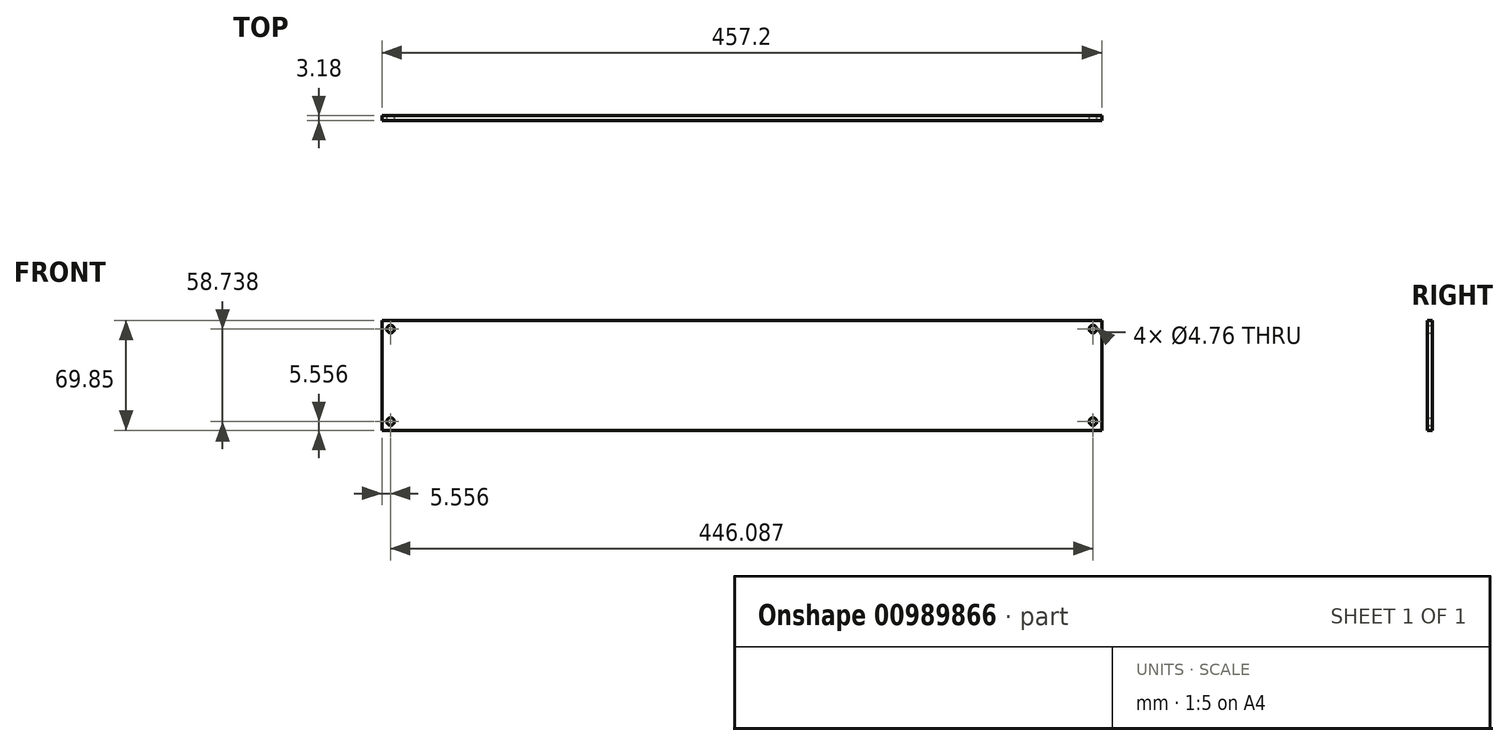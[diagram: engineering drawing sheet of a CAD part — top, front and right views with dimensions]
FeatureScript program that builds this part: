
annotation { "Feature Type Name" : "Feature", "Feature Type Description" : "" }
export const myFeature = defineFeature(function(context is Context, id is Id, definition is map)
    precondition{}
    {
        {
            var Q0;
            Q0=qCreatedBy(makeId("Right.planeOp"),FACE);
            var sketch = newSketch(context, id + "F0", { "sketchPlane" : qUnion([Q0])});
            skLineSegment(sketch, "E0", {"start": v(0, 0) * mm, "end": v(0, 69.85) * mm});
            skLineSegment(sketch, "E1", {"start": v(0, 69.85) * mm, "end": v(3.17, 69.85) * mm});
            skLineSegment(sketch, "E2", {"start": v(3.17, 69.85) * mm, "end": v(3.17, 0) * mm});
            skLineSegment(sketch, "E3", {"start": v(0, 0) * mm, "end": v(3.17, 0) * mm});
            skSolve(sketch);
        }
        {
            var Q0;
            Q0=makeQuery(id+"F0.imprint","IMPRINT",FACE,{"disambiguationData":[TD([[makeQuery(id+"F0.imprint","IMPRINT",EDGE,{"derivedFrom":sQuery(id+"F0.wireOp",EDGE,"E0")}),-1.0]])]});
            extrude(context, id + "F1", {"entities" : qUnion([Q0]), "depth" : 457.2 * mm, "offsetDistance" : 25.4 * mm});
        }
        {
            var Q0;
            Q0=makeQuery(id+"F1.opExtrude","SWEPT_FACE",FACE,{"disambiguationData":[OSD([sQuery(id+"F0.wireOp",EDGE,"E2")])]});
            var sketch = newSketch(context, id + "F2", { "sketchPlane" : qUnion([Q0])});
            skCircle(sketch, "E4", {"center": v(-5.56, 64.3) * mm, "radius": 2.38 * mm});
            skCircle(sketch, "E5", {"center": v(-5.56, 5.56) * mm, "radius": 2.38 * mm});
            skCircle(sketch, "E6", {"center": v(-451.64, 64.3) * mm, "radius": 2.38 * mm});
            skCircle(sketch, "E7", {"center": v(-451.64, 5.56) * mm, "radius": 2.38 * mm});
            skSolve(sketch);
        }
        {
            var Q0;
            Q0 = qSketchRegion(id + "F2", true);
            extrude(context, id + "F3", {"entities" : qUnion([Q0]), "operationType" : NewBodyOperationType.REMOVE, "endBound" : BoundingType.THROUGH_ALL, "oppositeDirection" : true, "depth" : 25.4 * mm, "offsetDistance" : 25.4 * mm});
        }
    });
